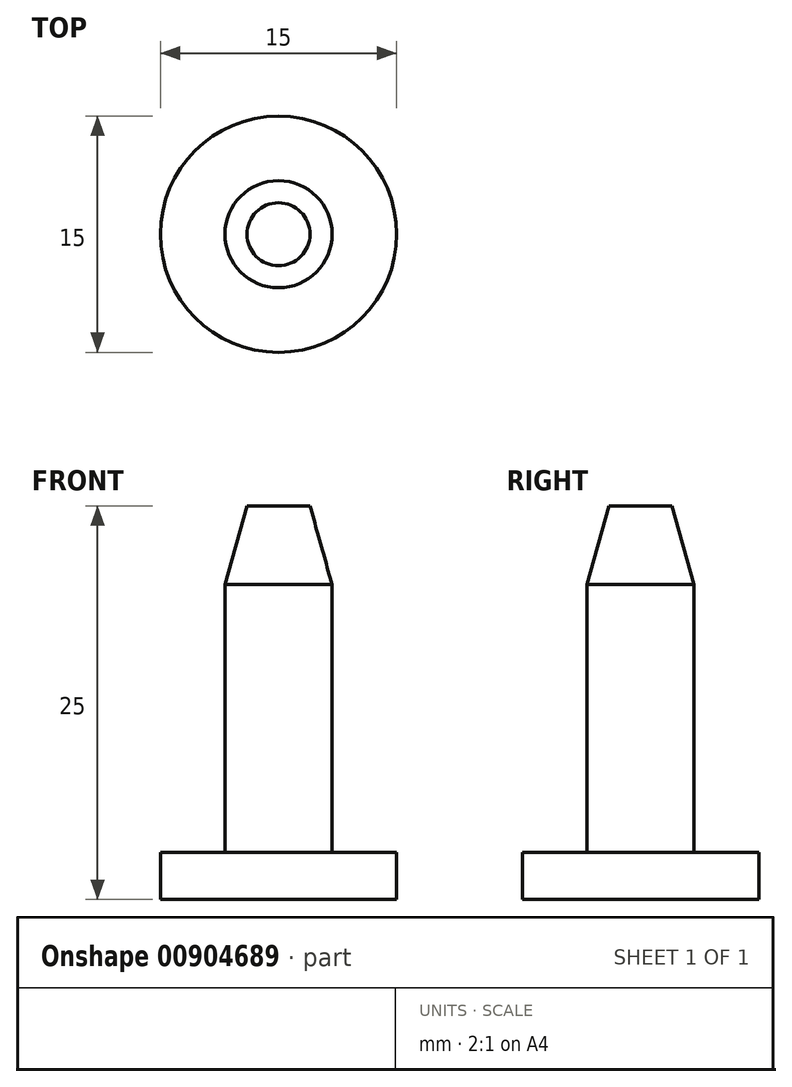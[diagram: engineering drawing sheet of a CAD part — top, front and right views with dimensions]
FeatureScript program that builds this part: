
annotation { "Feature Type Name" : "Feature", "Feature Type Description" : "" }
export const myFeature = defineFeature(function(context is Context, id is Id, definition is map)
    precondition{}
    {
        {
            var Q0;
            Q0=qCreatedBy(makeId("Front.planeOp"),FACE);
            var sketch = newSketch(context, id + "F0", { "sketchPlane" : qUnion([Q0])});
            skLineSegment(sketch, "E0", {"start": v(0, 57.78) * mm, "end": v(0, -9.03) * mm, "construction": true});
            skLineSegment(sketch, "E1", {"start": v(-3.4, 0) * mm, "end": v(-3.4, 20) * mm});
            skLineSegment(sketch, "E2", {"start": v(-3.4, 20) * mm, "end": v(-2, 25) * mm});
            skLineSegment(sketch, "E3", {"start": v(-2, 25) * mm, "end": v(0, 25) * mm});
            skLineSegment(sketch, "E4", {"start": v(-3.4, 0) * mm, "end": v(0, 0) * mm});
            skLineSegment(sketch, "E5", {"start": v(0, 0) * mm, "end": v(0, 25) * mm});
            skSolve(sketch);
        }
        {
            var Q0;
            Q0 = qSketchRegion(id + "F0", true);
            var Q1;
            Q1=sQuery(id+"F0.wireOp",EDGE,"E0");
            revolve(context, id + "F1", {"surfaceOperationType" : NewSurfaceOperationType.NEW, "entities" : qUnion([Q0]), "axis" : qUnion([Q1]), "revolveType" : RevolveType.FULL});
        }
        {
            var Q0;
            Q0=makeQuery(id+"F1.opRevolve","SWEPT_FACE",FACE,{"disambiguationData":[OSD([sQuery(id+"F0.wireOp",EDGE,"E4")])]});
            var sketch = newSketch(context, id + "F2", { "sketchPlane" : qUnion([Q0])});
            skCircle(sketch, "E6", {"center": v(0, 0) * mm, "radius": 7.5 * mm});
            skSolve(sketch);
        }
        {
            var Q0;
            Q0 = qSketchRegion(id + "F2", true);
            extrude(context, id + "F3", {"entities" : qUnion([Q0]), "operationType" : NewBodyOperationType.ADD, "oppositeDirection" : true, "depth" : 3 * mm, "offsetDistance" : 25 * mm});
        }
    });
